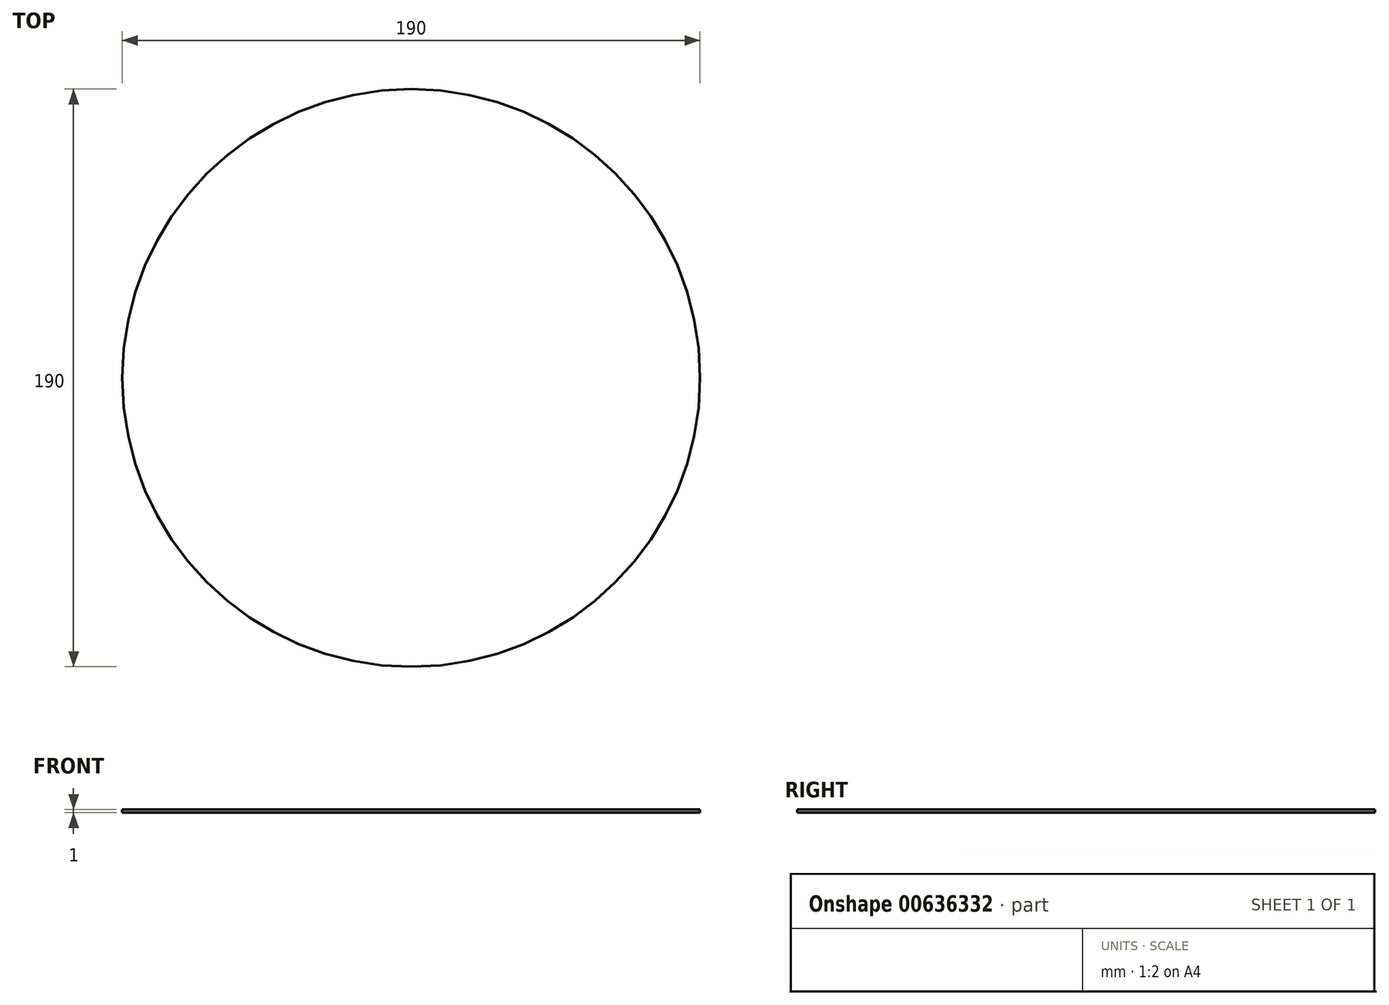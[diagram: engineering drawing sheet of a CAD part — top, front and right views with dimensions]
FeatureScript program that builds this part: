
annotation { "Feature Type Name" : "Feature", "Feature Type Description" : "" }
export const myFeature = defineFeature(function(context is Context, id is Id, definition is map)
    precondition{}
    {
        {
            var Q0;
            Q0=qCreatedBy(makeId("Top.planeOp"),FACE);
            var sketch = newSketch(context, id + "F0", { "sketchPlane" : qUnion([Q0])});
            skCircle(sketch, "E0", {"center": v(0, 0) * mm, "radius": 95 * mm});
            skSolve(sketch);
        }
        {
            var Q0;
            Q0 = qSketchRegion(id + "F0", true);
            extrude(context, id + "F1", {"entities" : qUnion([Q0]), "depth" : 1 * mm, "offsetDistance" : 25 * mm});
        }
    });
